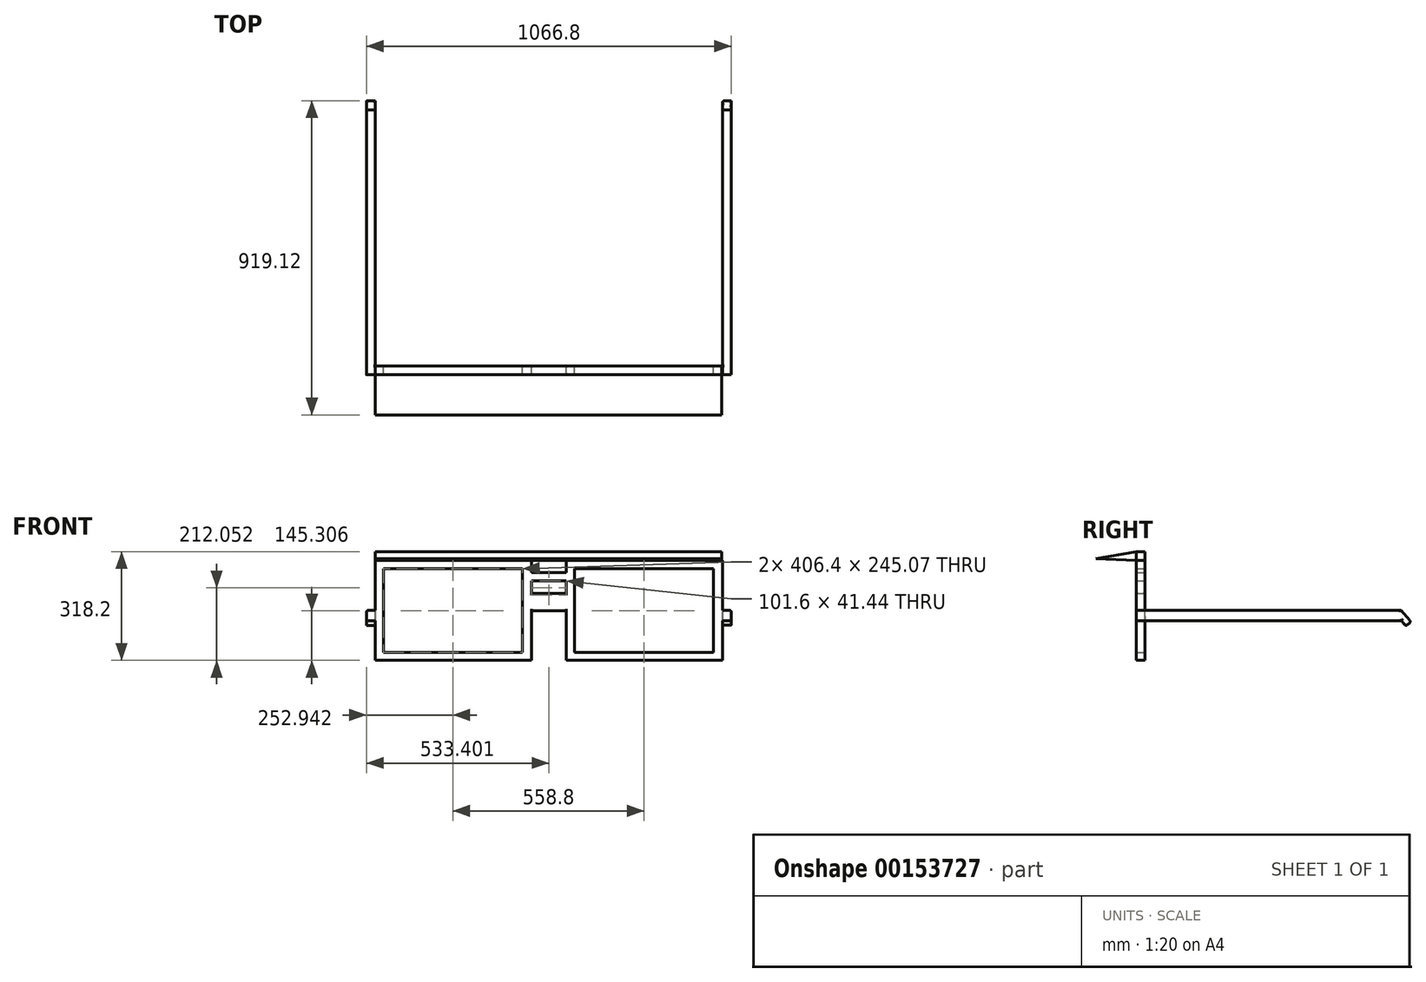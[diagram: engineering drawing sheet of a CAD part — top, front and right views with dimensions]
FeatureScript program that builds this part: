
annotation { "Feature Type Name" : "Feature", "Feature Type Description" : "" }
export const myFeature = defineFeature(function(context is Context, id is Id, definition is map)
    precondition{}
    {
        {
            var Q0;
            Q0=qCreatedBy(makeId("Front.planeOp"),FACE);
            var sketch = newSketch(context, id + "F0", { "sketchPlane" : qUnion([Q0])});
            skLineSegment(sketch, "E0.bottom", {"start": v(-730.29, 245.07) * mm, "end": v(-323.89, 245.07) * mm});
            skLineSegment(sketch, "E0.top", {"start": v(-730.29, 0) * mm, "end": v(-323.89, 0) * mm});
            skLineSegment(sketch, "E0.left", {"start": v(-730.29, 245.07) * mm, "end": v(-730.29, 0) * mm});
            skLineSegment(sketch, "E0.right", {"start": v(-323.89, 245.07) * mm, "end": v(-323.89, 0) * mm});
            skLineSegment(sketch, "E1", {"start": v(-323.89, 173.64) * mm, "end": v(-171.49, 173.64) * mm});
            skLineSegment(sketch, "E2.bottom", {"start": v(-171.49, 245.07) * mm, "end": v(234.91, 245.07) * mm});
            skLineSegment(sketch, "E2.top", {"start": v(-171.49, 0) * mm, "end": v(234.91, 0) * mm});
            skLineSegment(sketch, "E2.left", {"start": v(-171.49, 245.07) * mm, "end": v(-171.49, 0) * mm});
            skLineSegment(sketch, "E2.right", {"start": v(234.91, 245.07) * mm, "end": v(234.91, 0) * mm});
            skLineSegment(sketch, "E3", {"start": v(-323.89, 122.54) * mm, "end": v(-171.49, 122.54) * mm});
            skLineSegment(sketch, "E4.bottom", {"start": v(-754.63, -22.77) * mm, "end": v(-297.43, -22.77) * mm});
            skLineSegment(sketch, "E4.top", {"start": v(-754.63, 270.03) * mm, "end": v(-297.43, 270.03) * mm});
            skLineSegment(sketch, "E4.left", {"start": v(-754.63, -22.77) * mm, "end": v(-754.63, 270.03) * mm});
            skLineSegment(sketch, "E4.right", {"start": v(-297.43, -22.77) * mm, "end": v(-297.43, 270.03) * mm});
            skLineSegment(sketch, "E5.MirrorCS", {"start": v(261.37, -22.77) * mm, "end": v(-195.83, -22.77) * mm});
            skLineSegment(sketch, "E6.MirrorCS", {"start": v(261.37, -22.77) * mm, "end": v(261.37, 270.03) * mm});
            skLineSegment(sketch, "E7.MirrorCS", {"start": v(261.37, 270.03) * mm, "end": v(-195.83, 270.03) * mm});
            skLineSegment(sketch, "E8.MirrorCS", {"start": v(-195.83, -22.77) * mm, "end": v(-195.83, 270.03) * mm});
            skLineSegment(sketch, "E9", {"start": v(-297.43, 234.6) * mm, "end": v(-195.83, 234.6) * mm});
            skLineSegment(sketch, "E10", {"start": v(-297.43, 210) * mm, "end": v(-195.83, 210) * mm});
            skSolve(sketch);
        }
        {
            var Q0;
            Q0 = qSketchRegion(id + "F0", true);
            extrude(context, id + "F1", {"entities" : qUnion([Q0]), "depth" : 25.4 * mm});
        }
        {
            var Q0;
            Q0=makeQuery(id+"F1.opExtrude","SWEPT_FACE",FACE,{"disambiguationData":[OSD([sQuery(id+"F0.wireOp",EDGE,"E4.left")])]});
            var sketch = newSketch(context, id + "F2", { "sketchPlane" : qUnion([Q0])});
            skPoint(sketch, "E11.endSnap0", {"position": v(25.4, 123.63) * mm});
            skLineSegment(sketch, "E12", {"start": v(25.4, 123.63) * mm, "end": v(-749.22, 123.63) * mm});
            skLineSegment(sketch, "E13", {"start": v(-749.22, 123.63) * mm, "end": v(-778.26, 90.43) * mm});
            skLineSegment(sketch, "E14", {"start": v(-778.26, 90.43) * mm, "end": v(-763.74, 77.73) * mm});
            skPoint(sketch, "E14.endSnap0", {"position": v(-763.74, 107.03) * mm});
            skLineSegment(sketch, "E15", {"start": v(-763.74, 77.73) * mm, "end": v(-750.74, 92.6) * mm});
            skLineSegment(sketch, "E16", {"start": v(-750.74, 92.6) * mm, "end": v(25.4, 92.6) * mm});
            skSolve(sketch);
        }
        {
            var Q0;
            Q0 = qSketchRegion(id + "F2", true);
            var Q1;
            {var subQ1=sQuery(id+"F2.wireOp",EDGE,"E13");Q1=makeQuery(id+"F2.imprint","IMPRINT",FACE,{"disambiguationData":[TD([[makeQuery(id+"F2.imprint","IMPRINT",EDGE,{"derivedFrom":subQ1}),1.0]])]});}
            var Q2;
            {var subQ0=sQuery(id+"F2.wireOp",EDGE,"E12");var subQ1=sQuery(id+"F0.wireOp",EDGE,"E4.left");var subQ2=makeQuery(id+"F1.opExtrude","CAP_EDGE",EDGE,{"disambiguationData":[OSD([subQ1])],"isStart":false});var subQ3=makeQuery(id+"F2.imprint","INTERSECT",VERTEX,{"derivedFrom":[subQ2,subQ0]});Q2=makeQuery(id+"F2.imprint","IMPRINT",FACE,{"disambiguationData":[TD([[makeQuery(id+"F2.imprint","IMPRINT",EDGE,{"disambiguationData":[TD([[subQ3,-1.0]])],"derivedFrom":subQ0}),1.0]])]});}
            extrude(context, id + "F3", {"entities" : qUnion([Q0, Q1, Q2]), "operationType" : NewBodyOperationType.ADD, "depth" : 25.4 * mm});
        }
        {
            var Q0;
            Q0=makeQuery(id+"F1.opExtrude","SWEPT_FACE",FACE,{"disambiguationData":[OSD([sQuery(id+"F0.wireOp",EDGE,"E6.MirrorCS")])]});
            var sketch = newSketch(context, id + "F4", { "sketchPlane" : qUnion([Q0])});
            skLineSegment(sketch, "E17", {"start": v(0, 123.63) * mm, "end": v(749.22, 123.63) * mm});
            skLineSegment(sketch, "E18", {"start": v(749.22, 123.63) * mm, "end": v(778.23, 90.49) * mm});
            skLineSegment(sketch, "E19", {"start": v(778.23, 90.49) * mm, "end": v(763.7, 77.78) * mm});
            skLineSegment(sketch, "E20", {"start": v(763.7, 77.78) * mm, "end": v(750.74, 92.6) * mm});
            skLineSegment(sketch, "E21", {"start": v(750.74, 92.6) * mm, "end": v(0, 92.6) * mm});
            skLineSegment(sketch, "E22", {"start": v(0, 123.63) * mm, "end": v(-25.4, 123.63) * mm});
            skLineSegment(sketch, "E23", {"start": v(0, 92.6) * mm, "end": v(-25.4, 92.6) * mm});
            skSolve(sketch);
        }
        {
            var Q0;
            Q0 = qSketchRegion(id + "F4", true);
            var Q1;
            {var subQ0=sQuery(id+"F4.wireOp",EDGE,"E22");Q1=makeQuery(id+"F4.imprint","IMPRINT",FACE,{"disambiguationData":[TD([[makeQuery(id+"F4.imprint","IMPRINT",EDGE,{"derivedFrom":subQ0}),1.0]])]});}
            var Q2;
            {var subQ1=sQuery(id+"F4.wireOp",EDGE,"E17");Q2=makeQuery(id+"F4.imprint","IMPRINT",FACE,{"disambiguationData":[TD([[makeQuery(id+"F4.imprint","IMPRINT",EDGE,{"derivedFrom":subQ1}),-1.0]])]});}
            extrude(context, id + "F5", {"entities" : qUnion([Q0, Q1, Q2]), "operationType" : NewBodyOperationType.ADD, "depth" : 25.4 * mm});
        }
        {
            var Q0;
            Q0=makeQuery(id+"F1.opExtrude","SWEPT_FACE",FACE,{"disambiguationData":[OSD([sQuery(id+"F0.wireOp",EDGE,"E4.top")])]});
            var sketch = newSketch(context, id + "F6", { "sketchPlane" : qUnion([Q0])});
            skLineSegment(sketch, "E24", {"start": v(-754.63, 0) * mm, "end": v(259.42, 0) * mm});
            skLineSegment(sketch, "E25", {"start": v(259.42, 0) * mm, "end": v(259.42, -25.23) * mm});
            skLineSegment(sketch, "E26", {"start": v(259.42, -25.23) * mm, "end": v(-754.63, -25.4) * mm});
            skLineSegment(sketch, "E27", {"start": v(-754.63, -25.4) * mm, "end": v(-754.63, 0) * mm});
            skSolve(sketch);
        }
        {
            var Q0;
            Q0 = qSketchRegion(id + "F6", true);
            extrude(context, id + "F7", {"entities" : qUnion([Q0]), "operationType" : NewBodyOperationType.ADD, "depth" : 25.4 * mm});
        }
        {
            var Q0;
            {var subQ8=sQuery(id+"F0.wireOp",EDGE,"E4.left");var subQ9=sQuery(id+"F0.wireOp",EDGE,"E4.top");Q0=makeQuery(id+"F7.boolean.opBoolean","MERGE",FACE,{"derivedFrom":[makeQuery(id+"F3.boolean.opBoolean","SPLIT",FACE,{"disambiguationData":[TD([makeQuery(id+"F1.opExtrude","SWEPT_FACE",FACE,{"disambiguationData":[OSD([subQ9])]})])],"derivedFrom":makeQuery(id+"F1.opExtrude","SWEPT_FACE",FACE,{"disambiguationData":[OSD([subQ8])]})}),makeQuery(id+"F7.opExtrude","SWEPT_FACE",FACE,{"disambiguationData":[OSD([sQuery(id+"F6.wireOp",EDGE,"E27")])]})]});}
            var sketch = newSketch(context, id + "F8", { "sketchPlane" : qUnion([Q0])});
            skLineSegment(sketch, "E28", {"start": v(25.4, 295.43) * mm, "end": v(142.95, 274.4) * mm});
            skLineSegment(sketch, "E29", {"start": v(142.95, 274.4) * mm, "end": v(25.4, 270.03) * mm});
            skSolve(sketch);
        }
        {
            var Q0;
            Q0 = qSketchRegion(id + "F8", true);
            var Q1;
            Q1=makeQuery(id+"F8.imprint","IMPRINT",FACE,{"disambiguationData":[TD([[makeQuery(id+"F8.imprint","IMPRINT",EDGE,{"derivedFrom":sQuery(id+"F8.wireOp",EDGE,"E28")}),-1.0]])]});
            extrude(context, id + "F9", {"entities" : qUnion([Q0, Q1]), "oppositeDirection" : true, "depth" : 1014.1 * mm});
        }
        {
            var Q0;
            Q0=makeQuery(id+"F1.opExtrude","CAP_EDGE",EDGE,{"disambiguationData":[OSD([sQuery(id+"F0.wireOp",EDGE,"E1")])],"isStart":false});
            var Q1;
            Q1=makeQuery(id+"F1.opExtrude","CAP_EDGE",EDGE,{"disambiguationData":[OSD([sQuery(id+"F0.wireOp",EDGE,"E3")])],"isStart":false});
            var Q2;
            Q2=makeQuery(id+"F1.opExtrude","CAP_EDGE",EDGE,{"disambiguationData":[OSD([sQuery(id+"F0.wireOp",EDGE,"E1")])],"isStart":true});
            var Q3;
            Q3=makeQuery(id+"F1.opExtrude","CAP_EDGE",EDGE,{"disambiguationData":[OSD([sQuery(id+"F0.wireOp",EDGE,"E3")])],"isStart":true});
            fillet(context, id + "F10", {"entities" : qUnion([Q0, Q1, Q2, Q3]), "radius" : 5.08 * mm, "tangentPropagation" : true, "allowEdgeOverflow" : false});
        }
        {
            var Q0;
            {var subQ0=sQuery(id+"F2.wireOp",EDGE,"E12");Q0=makeQuery(id+"F3.boolean.opBoolean","SPLIT",EDGE,{"disambiguationData":[topologyDisambiguationEdgeConnected([makeQuery(id+"F3.opExtrude","CAP_FACE",FACE,{"disambiguationData":[OSD([sQuery(id+"F0.wireOp",EDGE,"E4.left"),subQ0,sQuery(id+"F2.wireOp",EDGE,"E13"),sQuery(id+"F2.wireOp",EDGE,"E14"),sQuery(id+"F2.wireOp",EDGE,"E15"),sQuery(id+"F2.wireOp",EDGE,"E16")])],"isStart":true})])],"derivedFrom":makeQuery(id+"F3.opExtrude","CAP_EDGE",EDGE,{"disambiguationData":[OSD([subQ0])],"isStart":true})});}
            var Q1;
            Q1=makeQuery(id+"F3.opExtrude","CAP_EDGE",EDGE,{"disambiguationData":[OSD([sQuery(id+"F2.wireOp",EDGE,"E12")])],"isStart":false});
            var Q2;
            Q2=makeQuery(id+"F3.opExtrude","CAP_EDGE",EDGE,{"disambiguationData":[OSD([sQuery(id+"F2.wireOp",EDGE,"E16")])],"isStart":false});
            var Q3;
            {var subQ0=sQuery(id+"F2.wireOp",EDGE,"E16");Q3=makeQuery(id+"F3.boolean.opBoolean","SPLIT",EDGE,{"disambiguationData":[topologyDisambiguationEdgeConnected([makeQuery(id+"F3.opExtrude","CAP_FACE",FACE,{"disambiguationData":[OSD([sQuery(id+"F0.wireOp",EDGE,"E4.left"),sQuery(id+"F2.wireOp",EDGE,"E12"),sQuery(id+"F2.wireOp",EDGE,"E13"),sQuery(id+"F2.wireOp",EDGE,"E14"),sQuery(id+"F2.wireOp",EDGE,"E15"),subQ0])],"isStart":true})])],"derivedFrom":makeQuery(id+"F3.opExtrude","CAP_EDGE",EDGE,{"disambiguationData":[OSD([subQ0])],"isStart":true})});}
            var Q4;
            Q4=makeQuery(id+"F3.opExtrude","SWEPT_EDGE",EDGE,{"disambiguationData":[OSD([sQuery(id+"F2.wireOp",EDGE,"E13"),sQuery(id+"F2.wireOp",EDGE,"E14")])]});
            var Q5;
            Q5=makeQuery(id+"F3.opExtrude","CAP_EDGE",EDGE,{"disambiguationData":[OSD([sQuery(id+"F2.wireOp",EDGE,"E13")])],"isStart":false});
            var Q6;
            Q6=makeQuery(id+"F3.opExtrude","SWEPT_EDGE",EDGE,{"disambiguationData":[OSD([sQuery(id+"F2.wireOp",EDGE,"E14"),sQuery(id+"F2.wireOp",EDGE,"E15")])]});
            var Q7;
            Q7=makeQuery(id+"F3.opExtrude","CAP_EDGE",EDGE,{"disambiguationData":[OSD([sQuery(id+"F2.wireOp",EDGE,"E13")])],"isStart":true});
            fillet(context, id + "F11", {"entities" : qUnion([Q0, Q1, Q2, Q3, Q4, Q5, Q6, Q7]), "radius" : 5.08 * mm, "tangentPropagation" : true, "allowEdgeOverflow" : false});
        }
        {
            var Q0;
            Q0=makeQuery(id+"F5.opExtrude","CAP_EDGE",EDGE,{"disambiguationData":[OSD([sQuery(id+"F4.wireOp",EDGE,"E17"),sQuery(id+"F4.wireOp",EDGE,"E22")])],"isStart":false});
            var Q1;
            Q1=makeQuery(id+"F5.opExtrude","CAP_EDGE",EDGE,{"disambiguationData":[OSD([sQuery(id+"F4.wireOp",EDGE,"E21"),sQuery(id+"F4.wireOp",EDGE,"E23")])],"isStart":false});
            var Q2;
            {var subQ0=sQuery(id+"F4.wireOp",EDGE,"E22");var subQ1=sQuery(id+"F4.wireOp",EDGE,"E17");Q2=makeQuery(id+"F5.boolean.opBoolean","SPLIT",EDGE,{"disambiguationData":[topologyDisambiguationEdgeConnected([makeQuery(id+"F5.opExtrude","CAP_FACE",FACE,{"disambiguationData":[OSD([sQuery(id+"F0.wireOp",EDGE,"E6.MirrorCS"),subQ1,sQuery(id+"F4.wireOp",EDGE,"E18"),sQuery(id+"F4.wireOp",EDGE,"E19"),sQuery(id+"F4.wireOp",EDGE,"E20"),sQuery(id+"F4.wireOp",EDGE,"E21"),subQ0,sQuery(id+"F4.wireOp",EDGE,"E23")])],"isStart":true})])],"derivedFrom":makeQuery(id+"F5.opExtrude","CAP_EDGE",EDGE,{"disambiguationData":[OSD([subQ1,subQ0])],"isStart":true})});}
            var Q3;
            {var subQ0=sQuery(id+"F4.wireOp",EDGE,"E23");var subQ1=sQuery(id+"F4.wireOp",EDGE,"E21");Q3=makeQuery(id+"F5.boolean.opBoolean","SPLIT",EDGE,{"disambiguationData":[topologyDisambiguationEdgeConnected([makeQuery(id+"F5.opExtrude","CAP_FACE",FACE,{"disambiguationData":[OSD([sQuery(id+"F0.wireOp",EDGE,"E6.MirrorCS"),sQuery(id+"F4.wireOp",EDGE,"E17"),sQuery(id+"F4.wireOp",EDGE,"E18"),sQuery(id+"F4.wireOp",EDGE,"E19"),sQuery(id+"F4.wireOp",EDGE,"E20"),subQ1,sQuery(id+"F4.wireOp",EDGE,"E22"),subQ0])],"isStart":true})])],"derivedFrom":makeQuery(id+"F5.opExtrude","CAP_EDGE",EDGE,{"disambiguationData":[OSD([subQ1,subQ0])],"isStart":true})});}
            var Q4;
            Q4=makeQuery(id+"F5.opExtrude","CAP_EDGE",EDGE,{"disambiguationData":[OSD([sQuery(id+"F4.wireOp",EDGE,"E18")])],"isStart":false});
            var Q5;
            Q5=makeQuery(id+"F5.opExtrude","SWEPT_EDGE",EDGE,{"disambiguationData":[OSD([sQuery(id+"F4.wireOp",EDGE,"E19"),sQuery(id+"F4.wireOp",EDGE,"E20")])]});
            var Q6;
            Q6=makeQuery(id+"F5.opExtrude","CAP_EDGE",EDGE,{"disambiguationData":[OSD([sQuery(id+"F4.wireOp",EDGE,"E20")])],"isStart":false});
            var Q7;
            Q7=makeQuery(id+"F5.opExtrude","SWEPT_EDGE",EDGE,{"disambiguationData":[OSD([sQuery(id+"F4.wireOp",EDGE,"E18"),sQuery(id+"F4.wireOp",EDGE,"E19")])]});
            var Q8;
            Q8=makeQuery(id+"F5.opExtrude","CAP_EDGE",EDGE,{"disambiguationData":[OSD([sQuery(id+"F4.wireOp",EDGE,"E18")])],"isStart":true});
            var Q9;
            Q9=makeQuery(id+"F5.opExtrude","CAP_EDGE",EDGE,{"disambiguationData":[OSD([sQuery(id+"F4.wireOp",EDGE,"E19")])],"isStart":true});
            fillet(context, id + "F12", {"entities" : qUnion([Q0, Q1, Q2, Q3, Q4, Q5, Q6, Q7, Q8, Q9]), "radius" : 5.08 * mm, "tangentPropagation" : true, "allowEdgeOverflow" : false});
        }
    });
